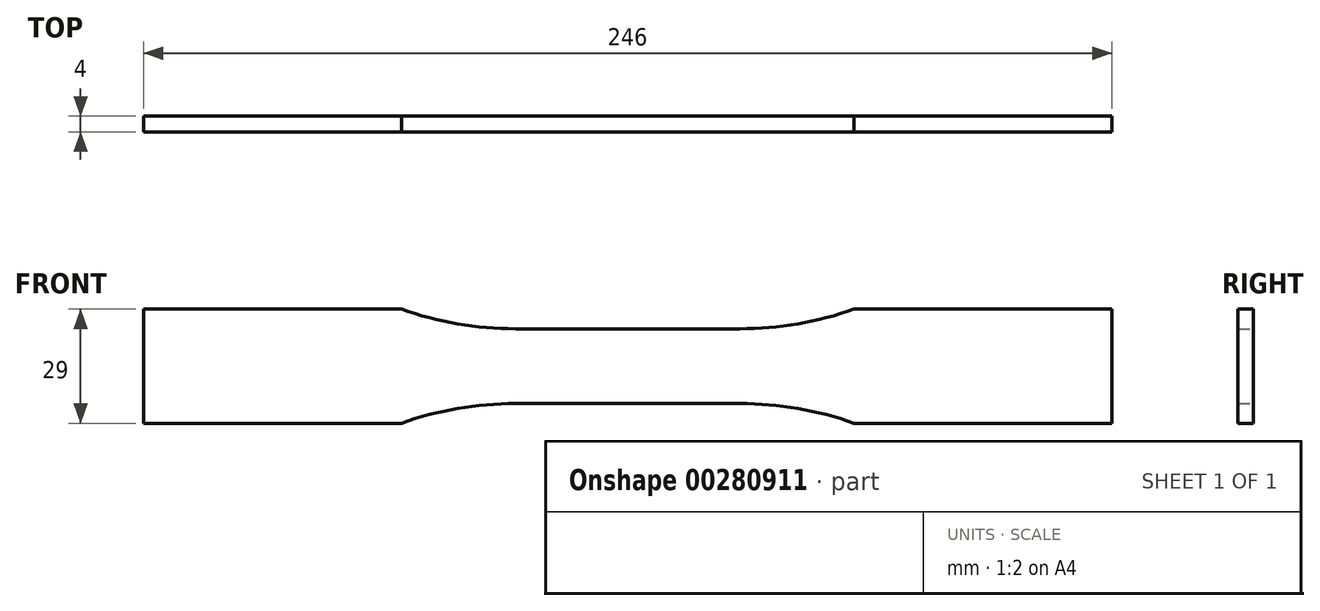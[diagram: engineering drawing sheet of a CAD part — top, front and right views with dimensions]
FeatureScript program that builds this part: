
annotation { "Feature Type Name" : "Feature", "Feature Type Description" : "" }
export const myFeature = defineFeature(function(context is Context, id is Id, definition is map)
    precondition{}
    {
        {
            var Q0;
            Q0=qCreatedBy(makeId("Front.planeOp"),FACE);
            var sketch = newSketch(context, id + "F0", { "sketchPlane" : qUnion([Q0])});
            skLineSegment(sketch, "E0", {"start": v(0, 9.5) * mm, "end": v(28.5, 9.5) * mm});
            skLineSegment(sketch, "E1", {"start": v(57.5, 14.5) * mm, "end": v(123, 14.5) * mm});
            skLineSegment(sketch, "E2", {"start": v(123, 14.5) * mm, "end": v(123, 0) * mm});
            skArc(sketch, "E3", {"start": v(28.5, 9.5) * mm, "mid": v(43.21, 10.76) * mm, "end": v(57.5, 14.5) * mm});
            skLineSegment(sketch, "E4.MirrorCS", {"start": v(57.5, -14.5) * mm, "end": v(123, -14.5) * mm});
            skArc(sketch, "E5.MirrorCS", {"start": v(28.5, -9.5) * mm, "mid": v(43.21, -10.76) * mm, "end": v(57.5, -14.5) * mm});
            skLineSegment(sketch, "E6.MirrorCS", {"start": v(123, -14.5) * mm, "end": v(123, 0) * mm});
            skLineSegment(sketch, "E7.MirrorCS", {"start": v(0, -9.5) * mm, "end": v(28.5, -9.5) * mm});
            skLineSegment(sketch, "E8.MirrorCS", {"start": v(0, -9.5) * mm, "end": v(-28.5, -9.5) * mm});
            skLineSegment(sketch, "E9.MirrorCS", {"start": v(-123, -14.5) * mm, "end": v(-123, 0) * mm});
            skLineSegment(sketch, "E10.MirrorCS", {"start": v(0, 9.5) * mm, "end": v(-28.5, 9.5) * mm});
            skLineSegment(sketch, "E11.MirrorCS", {"start": v(-57.5, 14.5) * mm, "end": v(-123, 14.5) * mm});
            skLineSegment(sketch, "E12.MirrorCS", {"start": v(-123, 14.5) * mm, "end": v(-123, 0) * mm});
            skArc(sketch, "E13.MirrorCS", {"start": v(-28.5, -9.5) * mm, "mid": v(-43.21, -10.76) * mm, "end": v(-57.5, -14.5) * mm});
            skLineSegment(sketch, "E14.MirrorCS", {"start": v(-57.5, -14.5) * mm, "end": v(-123, -14.5) * mm});
            skArc(sketch, "E15.MirrorCS", {"start": v(-28.5, 9.5) * mm, "mid": v(-43.21, 10.76) * mm, "end": v(-57.5, 14.5) * mm});
            skSolve(sketch);
        }
        {
            var Q0;
            Q0=qSketchRegion(id+"F0",true);
            extrude(context, id + "F1", {"entities" : qUnion([Q0]), "depth" : 4 * mm});
        }
    });
